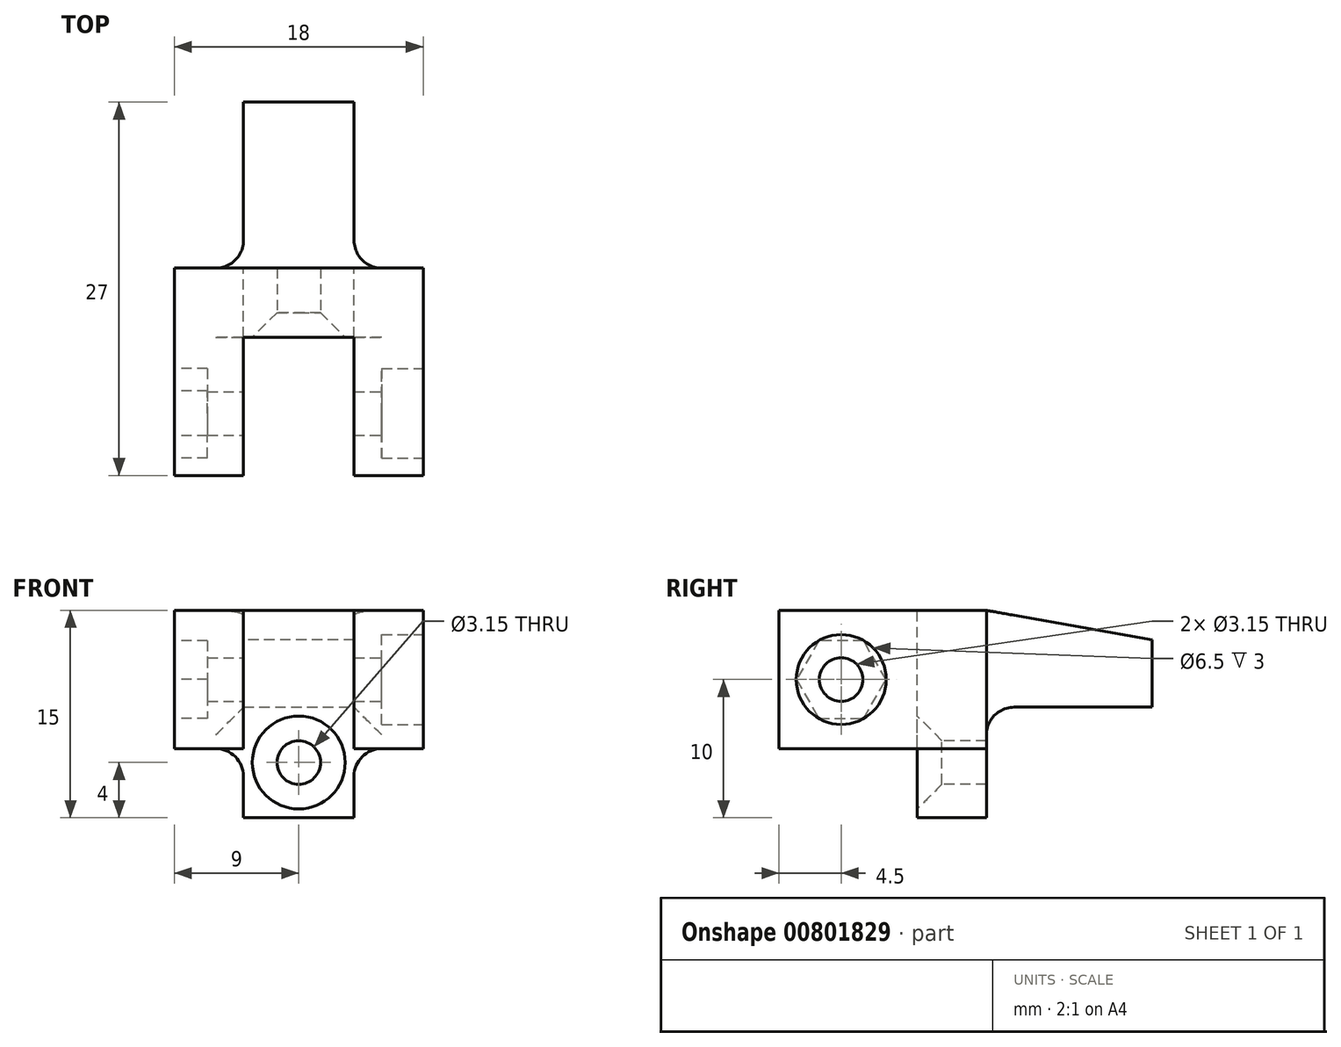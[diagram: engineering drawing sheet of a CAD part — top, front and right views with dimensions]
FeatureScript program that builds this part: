
annotation { "Feature Type Name" : "Feature", "Feature Type Description" : "" }
export const myFeature = defineFeature(function(context is Context, id is Id, definition is map)
    precondition{}
    {
        {
            var Q0;
            Q0=qCreatedBy(makeId("Front.planeOp"),FACE);
            var sketch = newSketch(context, id + "F0", { "sketchPlane" : qUnion([Q0])});
            skLineSegment(sketch, "E0.bottom", {"start": v(-9, 10) * mm, "end": v(9, 10) * mm});
            skLineSegment(sketch, "E0.top", {"start": v(-9, 0) * mm, "end": v(9, 0) * mm});
            skLineSegment(sketch, "E0.left", {"start": v(-9, 10) * mm, "end": v(-9, 0) * mm});
            skLineSegment(sketch, "E0.right", {"start": v(9, 10) * mm, "end": v(9, 0) * mm});
            skSolve(sketch);
        }
        {
            var Q0;
            Q0=makeQuery(id+"F0.imprint","IMPRINT",FACE,{"disambiguationData":[TD([[makeQuery(id+"F0.imprint","IMPRINT",EDGE,{"derivedFrom":sQuery(id+"F0.wireOp",EDGE,"E0.bottom")}),-1.0]])]});
            extrude(context, id + "F1", {"entities" : qUnion([Q0]), "depth" : 15 * mm, "offsetDistance" : 25 * mm});
        }
        {
            var Q0;
            Q0=makeQuery(id+"F1.opExtrude","CAP_FACE",FACE,{"disambiguationData":[OSD([sQuery(id+"F0.wireOp",EDGE,"E0.bottom"),sQuery(id+"F0.wireOp",EDGE,"E0.top"),sQuery(id+"F0.wireOp",EDGE,"E0.left"),sQuery(id+"F0.wireOp",EDGE,"E0.right")])],"isStart":false});
            var sketch = newSketch(context, id + "F2", { "sketchPlane" : qUnion([Q0])});
            skLineSegment(sketch, "E1.bottom", {"start": v(-4, 0) * mm, "end": v(4, 0) * mm});
            skLineSegment(sketch, "E1.top", {"start": v(-4, 10) * mm, "end": v(4, 10) * mm});
            skLineSegment(sketch, "E1.left", {"start": v(-4, 0) * mm, "end": v(-4, 10) * mm});
            skLineSegment(sketch, "E1.right", {"start": v(4, 0) * mm, "end": v(4, 10) * mm});
            skSolve(sketch);
        }
        {
            var Q0;
            Q0 = qSketchRegion(id + "F2", true);
            extrude(context, id + "F3", {"entities" : qUnion([Q0]), "operationType" : NewBodyOperationType.REMOVE, "oppositeDirection" : true, "depth" : 10 * mm, "offsetDistance" : 25 * mm});
        }
        {
            var Q0;
            Q0=makeQuery(id+"F1.opExtrude","SWEPT_FACE",FACE,{"disambiguationData":[OSD([sQuery(id+"F0.wireOp",EDGE,"E0.right")])]});
            var sketch = newSketch(context, id + "F4", { "sketchPlane" : qUnion([Q0])});
            skCircle(sketch, "E2", {"center": v(-10.5, 5) * mm, "radius": 1.5 * mm});
            skLineSegment(sketch, "E3", {"start": v(-15, 5) * mm, "end": v(0, 5) * mm, "construction": true});
            skSolve(sketch);
        }
        {
            var Q0;
            Q0=sQuery(id+"F4.wireOp",VERTEX,"E2.center");
            var Q1;
            Q1=makeQuery(id+"F1.opExtrude","SWEPT_BODY",BODY,{"disambiguationData":[OSD([sQuery(id+"F0.wireOp",EDGE,"E0.bottom"),sQuery(id+"F0.wireOp",EDGE,"E0.top"),sQuery(id+"F0.wireOp",EDGE,"E0.left"),sQuery(id+"F0.wireOp",EDGE,"E0.right")])]});
            hole(context, id + "F5", {"style" : HoleStyle.C_BORE, "endStyle" : HoleEndStyle.THROUGH, "standardTappedOrClearance" : lookupTablePath({ "standard" : "ISO", "fit" : "Close", "size" : "M3", "type" : "Clearance" }), "standardBlindInLast" : lookupTablePath({ "fit" : "Close", "standard" : "ISO", "size" : "M3", "type" : "Clearance" }), "holeDiameter" : 3.15 * mm, "cBoreDiameter" : 6.5 * mm, "cBoreDepth" : 3 * mm, "majorDiameter" : 5 * mm, "isTappedThrough" : true, "tappedDepth" : 12 * mm, "tapClearance" : 3, "locations" : qUnion([Q0]), "scope" : qUnion([Q1])});
        }
        {
            var Q0;
            Q0=makeQuery(id+"F1.opExtrude","SWEPT_FACE",FACE,{"disambiguationData":[OSD([sQuery(id+"F0.wireOp",EDGE,"E0.left")])]});
            var sketch = newSketch(context, id + "F6", { "sketchPlane" : qUnion([Q0])});
            skCircle(sketch, "E4.cCircle", {"center": v(10.5, 5) * mm, "radius": 2.8 * mm, "construction": true});
            skLineSegment(sketch, "E4.0", {"start": v(13.73, 5) * mm, "end": v(12.12, 2.2) * mm});
            skLineSegment(sketch, "E4.1", {"start": v(12.12, 2.2) * mm, "end": v(8.88, 2.2) * mm});
            skLineSegment(sketch, "E4.2", {"start": v(8.88, 2.2) * mm, "end": v(7.27, 5) * mm});
            skLineSegment(sketch, "E4.3", {"start": v(7.27, 5) * mm, "end": v(8.88, 7.8) * mm});
            skLineSegment(sketch, "E4.4", {"start": v(8.88, 7.8) * mm, "end": v(12.12, 7.8) * mm});
            skLineSegment(sketch, "E4.5", {"start": v(12.12, 7.8) * mm, "end": v(13.73, 5) * mm});
            skPoint(sketch, "E4.0.midPoint", {"position": v(12.92, 3.6) * mm});
            skSolve(sketch);
        }
        {
            var Q0;
            Q0 = qSketchRegion(id + "F6", true);
            extrude(context, id + "F7", {"entities" : qUnion([Q0]), "operationType" : NewBodyOperationType.REMOVE, "oppositeDirection" : true, "depth" : 2.4 * mm, "offsetDistance" : 25 * mm});
        }
        {
            var Q0;
            Q0=makeQuery(id+"F3.boolean.opBoolean","COPY",FACE,{"derivedFrom":makeQuery(id+"F3.opExtrude","CAP_FACE",FACE,{"disambiguationData":[OSD([sQuery(id+"F2.wireOp",EDGE,"E1.bottom"),sQuery(id+"F2.wireOp",EDGE,"E1.top"),sQuery(id+"F2.wireOp",EDGE,"E1.left"),sQuery(id+"F2.wireOp",EDGE,"E1.right")])],"isStart":false})});
            var sketch = newSketch(context, id + "F8", { "sketchPlane" : qUnion([Q0])});
            skLineSegment(sketch, "E5.bottom", {"start": v(4, 10) * mm, "end": v(-4, 10) * mm});
            skLineSegment(sketch, "E5.top", {"start": v(4, -5) * mm, "end": v(-4, -5) * mm});
            skLineSegment(sketch, "E5.left", {"start": v(4, 10) * mm, "end": v(4, -5) * mm});
            skLineSegment(sketch, "E5.right", {"start": v(-4, 10) * mm, "end": v(-4, -5) * mm});
            skSolve(sketch);
        }
        {
            var Q0;
            Q0 = qSketchRegion(id + "F8", true);
            extrude(context, id + "F9", {"entities" : qUnion([Q0]), "operationType" : NewBodyOperationType.ADD, "oppositeDirection" : true, "depth" : 17 * mm, "offsetDistance" : 25 * mm});
        }
        {
            var Q0;
            Q0=makeQuery(id+"F9.opExtrude","CAP_FACE",FACE,{"disambiguationData":[OSD([sQuery(id+"F8.wireOp",EDGE,"E5.bottom"),sQuery(id+"F8.wireOp",EDGE,"E5.top"),sQuery(id+"F8.wireOp",EDGE,"E5.left"),sQuery(id+"F8.wireOp",EDGE,"E5.right")])],"isStart":false});
            var sketch = newSketch(context, id + "F10", { "sketchPlane" : qUnion([Q0])});
            skLineSegment(sketch, "E6.bottom", {"start": v(4, 10) * mm, "end": v(-4, 10) * mm});
            skLineSegment(sketch, "E6.top", {"start": v(4, 7) * mm, "end": v(-4, 7) * mm});
            skLineSegment(sketch, "E6.left", {"start": v(4, 10) * mm, "end": v(4, 7) * mm});
            skLineSegment(sketch, "E6.right", {"start": v(-4, 10) * mm, "end": v(-4, 7) * mm});
            skLineSegment(sketch, "E7.bottom", {"start": v(4, -5) * mm, "end": v(-4, -5) * mm});
            skLineSegment(sketch, "E7.top", {"start": v(4, 3) * mm, "end": v(-4, 3) * mm});
            skLineSegment(sketch, "E7.left", {"start": v(4, -5) * mm, "end": v(4, 3) * mm});
            skLineSegment(sketch, "E7.right", {"start": v(-4, -5) * mm, "end": v(-4, 3) * mm});
            skSolve(sketch);
        }
        {
            var Q0;
            Q0=makeQuery(id+"F10.imprint","IMPRINT",FACE,{"disambiguationData":[TD([[makeQuery(id+"F10.imprint","IMPRINT",EDGE,{"derivedFrom":sQuery(id+"F10.wireOp",EDGE,"E7.bottom")}),1.0]])]});
            var Q1;
            {var subQ0=sQuery(id+"F0.wireOp",EDGE,"E0.left");var subQ1=sQuery(id+"F0.wireOp",EDGE,"E0.top");var subQ2=sQuery(id+"F0.wireOp",EDGE,"E0.bottom");Q1=makeQuery(id+"F9.boolean.opBoolean","SPLIT",FACE,{"disambiguationData":[TD([makeQuery(id+"F1.opExtrude","SWEPT_FACE",FACE,{"disambiguationData":[OSD([subQ0])]})])],"derivedFrom":makeQuery(id+"F1.opExtrude","CAP_FACE",FACE,{"disambiguationData":[OSD([subQ2,subQ1,subQ0,sQuery(id+"F0.wireOp",EDGE,"E0.right")])],"isStart":true})});}
            extrude(context, id + "F11", {"entities" : qUnion([Q0]), "operationType" : NewBodyOperationType.REMOVE, "endBound" : BoundingType.UP_TO_SURFACE, "oppositeDirection" : true, "depth" : 25 * mm, "endBoundEntityFace" : qUnion([Q1]), "offsetDistance" : 25 * mm});
        }
        {
            var Q0;
            Q0=makeQuery(id+"F9.boolean.opBoolean","MERGE",FACE,{"derivedFrom":[makeQuery(id+"F3.boolean.opBoolean","COPY",FACE,{"derivedFrom":makeQuery(id+"F3.opExtrude","CAP_FACE",FACE,{"disambiguationData":[OSD([sQuery(id+"F2.wireOp",EDGE,"E1.bottom"),sQuery(id+"F2.wireOp",EDGE,"E1.top"),sQuery(id+"F2.wireOp",EDGE,"E1.left"),sQuery(id+"F2.wireOp",EDGE,"E1.right")])],"isStart":false})}),makeQuery(id+"F9.opExtrude","CAP_FACE",FACE,{"disambiguationData":[OSD([sQuery(id+"F8.wireOp",EDGE,"E5.bottom"),sQuery(id+"F8.wireOp",EDGE,"E5.top"),sQuery(id+"F8.wireOp",EDGE,"E5.left"),sQuery(id+"F8.wireOp",EDGE,"E5.right")])],"isStart":true})]});
            var sketch = newSketch(context, id + "F12", { "sketchPlane" : qUnion([Q0])});
            skPoint(sketch, "E8", {"position": v(0, -1) * mm});
            skSolve(sketch);
        }
        {
            var Q0;
            Q0=sQuery(id+"F12.wireOp",VERTEX,"E8");
            var Q1;
            Q1=makeQuery(id+"F1.opExtrude","SWEPT_BODY",BODY,{"disambiguationData":[OSD([sQuery(id+"F0.wireOp",EDGE,"E0.bottom"),sQuery(id+"F0.wireOp",EDGE,"E0.top"),sQuery(id+"F0.wireOp",EDGE,"E0.left"),sQuery(id+"F0.wireOp",EDGE,"E0.right")])]});
            hole(context, id + "F13", {"style" : HoleStyle.C_SINK, "endStyle" : HoleEndStyle.THROUGH, "standardTappedOrClearance" : lookupTablePath({ "standard" : "ISO", "fit" : "Close", "size" : "M3", "type" : "Clearance" }), "standardBlindInLast" : lookupTablePath({ "fit" : "Close", "standard" : "ISO", "size" : "M3", "type" : "Clearance" }), "holeDiameter" : 3.15 * mm, "cSinkDiameter" : 6.72 * mm, "cSinkAngle" : 90 * degree, "majorDiameter" : 5 * mm, "isTappedThrough" : true, "tappedDepth" : 12 * mm, "tapClearance" : 3, "locations" : qUnion([Q0]), "scope" : qUnion([Q1])});
        }
        {
            var Q0;
            {var subQ1=sQuery(id+"F0.wireOp",EDGE,"E0.bottom");var subQ2=sQuery(id+"F8.wireOp",EDGE,"E5.right");Q0=makeQuery(id+"F11.boolean.opBoolean","SPLIT",FACE,{"disambiguationData":[TD([makeQuery(id+"F1.opExtrude","SWEPT_FACE",FACE,{"disambiguationData":[OSD([subQ1])]})])],"derivedFrom":makeQuery(id+"F9.opExtrude","SWEPT_FACE",FACE,{"disambiguationData":[OSD([subQ2])]})});}
            var sketch = newSketch(context, id + "F14", { "sketchPlane" : qUnion([Q0])});
            skLineSegment(sketch, "E9", {"start": v(0, 10) * mm, "end": v(-12, 7.88) * mm});
            skSolve(sketch);
        }
        {
            var Q0;
            {var subQ0=sQuery(id+"F14.wireOp",EDGE,"E9");Q0=makeQuery(id+"F14.imprint","IMPRINT",FACE,{"disambiguationData":[TD([[makeQuery(id+"F14.imprint","IMPRINT",EDGE,{"derivedFrom":subQ0}),-1.0]])]});}
            extrude(context, id + "F15", {"entities" : qUnion([Q0]), "operationType" : NewBodyOperationType.REMOVE, "oppositeDirection" : true, "depth" : 25 * mm, "offsetDistance" : 25 * mm});
        }
        {
            var Q0;
            Q0=makeQuery(id+"F9.boolean.opBoolean","INTERSECT",EDGE,{"derivedFrom":[makeQuery(id+"F1.opExtrude","SWEPT_FACE",FACE,{"disambiguationData":[OSD([sQuery(id+"F0.wireOp",EDGE,"E0.top")])]}),makeQuery(id+"F9.opExtrude","SWEPT_FACE",FACE,{"disambiguationData":[OSD([sQuery(id+"F8.wireOp",EDGE,"E5.right")])]})]});
            var Q1;
            Q1=makeQuery(id+"F11.boolean.opBoolean","COPY",EDGE,{"derivedFrom":makeQuery(id+"F11.opExtrude","CAP_EDGE",EDGE,{"disambiguationData":[OSD([sQuery(id+"F10.wireOp",EDGE,"E7.top")])],"isStart":false})});
            var Q2;
            Q2=makeQuery(id+"F9.boolean.opBoolean","INTERSECT",EDGE,{"derivedFrom":[makeQuery(id+"F1.opExtrude","CAP_FACE",FACE,{"disambiguationData":[OSD([sQuery(id+"F0.wireOp",EDGE,"E0.bottom"),sQuery(id+"F0.wireOp",EDGE,"E0.top"),sQuery(id+"F0.wireOp",EDGE,"E0.left"),sQuery(id+"F0.wireOp",EDGE,"E0.right")])],"isStart":true}),makeQuery(id+"F9.opExtrude","SWEPT_FACE",FACE,{"disambiguationData":[OSD([sQuery(id+"F8.wireOp",EDGE,"E5.right")])]})]});
            var Q3;
            Q3=makeQuery(id+"F9.boolean.opBoolean","INTERSECT",EDGE,{"derivedFrom":[makeQuery(id+"F1.opExtrude","SWEPT_FACE",FACE,{"disambiguationData":[OSD([sQuery(id+"F0.wireOp",EDGE,"E0.top")])]}),makeQuery(id+"F9.opExtrude","SWEPT_FACE",FACE,{"disambiguationData":[OSD([sQuery(id+"F8.wireOp",EDGE,"E5.left")])]})]});
            var Q4;
            Q4=makeQuery(id+"F9.boolean.opBoolean","INTERSECT",EDGE,{"derivedFrom":[makeQuery(id+"F1.opExtrude","CAP_FACE",FACE,{"disambiguationData":[OSD([sQuery(id+"F0.wireOp",EDGE,"E0.bottom"),sQuery(id+"F0.wireOp",EDGE,"E0.top"),sQuery(id+"F0.wireOp",EDGE,"E0.left"),sQuery(id+"F0.wireOp",EDGE,"E0.right")])],"isStart":true}),makeQuery(id+"F9.opExtrude","SWEPT_FACE",FACE,{"disambiguationData":[OSD([sQuery(id+"F8.wireOp",EDGE,"E5.left")])]})]});
            var Q5;
            Q5=makeQuery(id+"F11.boolean.opBoolean","COPY",EDGE,{"derivedFrom":makeQuery(id+"F11.opExtrude","SWEPT_EDGE",EDGE,{"disambiguationData":[OSD([sQuery(id+"F8.wireOp",EDGE,"E5.right"),sQuery(id+"F10.wireOp",EDGE,"E7.top"),sQuery(id+"F10.wireOp",EDGE,"E7.left")])]})});
            var Q6;
            Q6=makeQuery(id+"F11.boolean.opBoolean","COPY",EDGE,{"derivedFrom":makeQuery(id+"F11.opExtrude","SWEPT_EDGE",EDGE,{"disambiguationData":[OSD([sQuery(id+"F8.wireOp",EDGE,"E5.left"),sQuery(id+"F10.wireOp",EDGE,"E7.top"),sQuery(id+"F10.wireOp",EDGE,"E7.right")])]})});
            fillet(context, id + "F16", {"entities" : qUnion([Q0, Q1, Q2, Q3, Q4, Q5, Q6]), "radius" : 2 * mm, "tangentPropagation" : true, "allowEdgeOverflow" : false});
        }
    });
